# Revit family: Manual_Faucet-Service_Sink-Zurn-Z843M1
name_source: partatom
category: Plumbing Fixtures
units: mm (PartAtom-declared; Revit-internal decimal feet)

## family parameters
Cut with Voids When Loaded = No
Host = Face
Maintain Annotation Orientation = No
OmniClass Number = 23.45.55.17
OmniClass Title = Mixing Faucets
Part Type = Normal
Room Calculation Point = No
Round Connector Dimension = Use Radius
Shared = No

## types (1)
- Z843M1 (Wall-Mount, Sink Faucet with 8" Vacuum Breaker Spout)
    Activation Method = Manually Operated
    Aerator Flow Rate (GPM) = 1 GPM
    Assembly Code = D2010.60
    CW Connection = Yes
    CWFU = 1
    Centerset Distance = 8 "
    Default Elevation = 48 "
    Description = SINK FAUCET
    Distance Between Aerator And Wall = 9.125 "
    Distance Bwtween Wall Brace & Spout Axis = 13 "
    HW Connection = Yes
    HWFU = 1
    Inlet Connection Size (inch) = 0.5 "
    Main Material = Finishes - Zurn - Chromed Plated Brass
    Manufacturer = Zurn Water, LLC
    Manufacturer Brand = Zurn
    Model = Z843M1
    Modified Data = 01/12/2026
    Product Documentation Link = https://files.zurn.com
    Product Installation Sheet URL = https://files.zurn.com
    Product Page URL = https://www.zurn.com
    Product data URL = https://www.bimobject.com
    Repair Parts URL = https://files.zurn.com
    URL = https://www.zurn.com
    Vent Connection = No
    WFU = 0
    Waste Connection = No

## geometry (parser evidence)
native form markers: Sweep x8
no freeform markers — native parametric forms only
